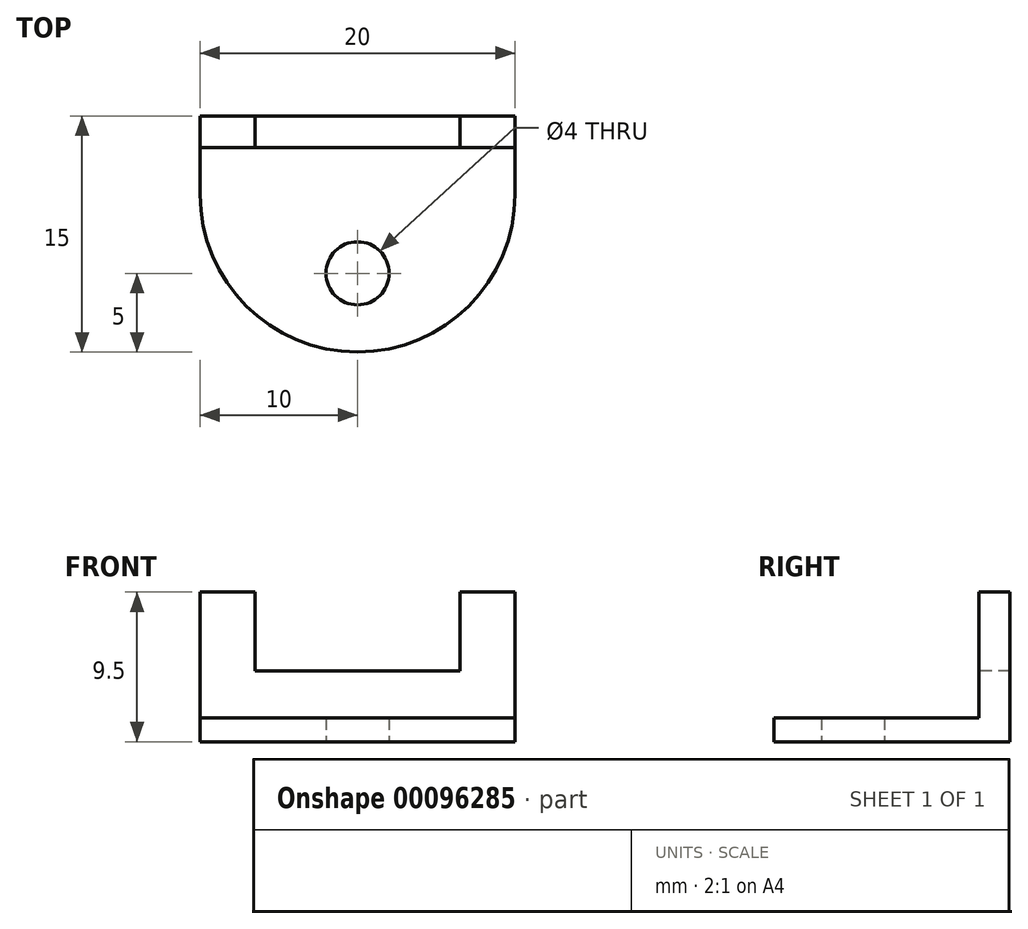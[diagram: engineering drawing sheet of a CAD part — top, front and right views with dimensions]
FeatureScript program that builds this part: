
annotation { "Feature Type Name" : "Feature", "Feature Type Description" : "" }
export const myFeature = defineFeature(function(context is Context, id is Id, definition is map)
    precondition{}
    {
        {
            var Q0;
            Q0=qCreatedBy(makeId("Top.planeOp"),FACE);
            var sketch = newSketch(context, id + "F0", { "sketchPlane" : qUnion([Q0])});
            skLineSegment(sketch, "E0.bottom", {"start": v(10, 2.5) * mm, "end": v(-10, 2.5) * mm});
            skLineSegment(sketch, "E0.top", {"start": v(10, -2.5) * mm, "end": v(-10, -2.5) * mm});
            skLineSegment(sketch, "E0.left", {"start": v(10, 2.5) * mm, "end": v(10, -2.5) * mm});
            skLineSegment(sketch, "E0.right", {"start": v(-10, 2.5) * mm, "end": v(-10, -2.5) * mm});
            skPoint(sketch, "E0.middle", {"position": v(0, 0) * mm});
            skArc(sketch, "E1", {"start": v(-10, -2.5) * mm, "mid": v(0, -12.5) * mm, "end": v(10, -2.5) * mm});
            skCircle(sketch, "E2", {"center": v(0, -7.5) * mm, "radius": 2 * mm});
            skSolve(sketch);
        }
        {
            var Q0;
            Q0=makeQuery(id+"F0.imprint","IMPRINT",FACE,{"disambiguationData":[TD([[makeQuery(id+"F0.imprint","IMPRINT",EDGE,{"derivedFrom":sQuery(id+"F0.wireOp",EDGE,"E0.bottom")}),1.0]])]});
            var Q1;
            Q1=makeQuery(id+"F0.imprint","IMPRINT",FACE,{"disambiguationData":[TD([[makeQuery(id+"F0.imprint","IMPRINT",EDGE,{"derivedFrom":sQuery(id+"F0.wireOp",EDGE,"E0.top")}),1.0]])]});
            extrude(context, id + "F1", {"entities" : qUnion([Q0, Q1]), "depth" : 1.5 * mm});
        }
        {
            var Q0;
            Q0=makeQuery(id+"F1.opExtrude","CAP_FACE",FACE,{"disambiguationData":[OSD([sQuery(id+"F0.wireOp",EDGE,"E0.bottom"),sQuery(id+"F0.wireOp",EDGE,"E0.left"),sQuery(id+"F0.wireOp",EDGE,"E0.right"),sQuery(id+"F0.wireOp",EDGE,"E1")])],"isStart":false});
            var sketch = newSketch(context, id + "F2", { "sketchPlane" : qUnion([Q0])});
            skLineSegment(sketch, "E3.bottom", {"start": v(-10, 2.5) * mm, "end": v(-6.5, 2.5) * mm});
            skLineSegment(sketch, "E3.top", {"start": v(-10, 0.5) * mm, "end": v(-6.5, 0.5) * mm});
            skLineSegment(sketch, "E3.left", {"start": v(-10, 2.5) * mm, "end": v(-10, 0.5) * mm});
            skLineSegment(sketch, "E3.right", {"start": v(-6.5, 2.5) * mm, "end": v(-6.5, 0.5) * mm});
            skLineSegment(sketch, "E4.MirrorCS", {"start": v(6.5, 2.5) * mm, "end": v(6.5, 0.5) * mm});
            skLineSegment(sketch, "E5.MirrorCS", {"start": v(10, 2.5) * mm, "end": v(10, 0.5) * mm});
            skLineSegment(sketch, "E6.MirrorCS", {"start": v(10, 0.5) * mm, "end": v(6.5, 0.5) * mm});
            skLineSegment(sketch, "E7.MirrorCS", {"start": v(10, 2.5) * mm, "end": v(6.5, 2.5) * mm});
            skSolve(sketch);
        }
        {
            var Q0;
            Q0=makeQuery(id+"F2.imprint","IMPRINT",FACE,{"disambiguationData":[TD([[makeQuery(id+"F2.imprint","IMPRINT",EDGE,{"derivedFrom":sQuery(id+"F2.wireOp",EDGE,"E3.bottom")}),1.0]])]});
            var Q1;
            Q1=makeQuery(id+"F2.imprint","IMPRINT",FACE,{"disambiguationData":[TD([[makeQuery(id+"F2.imprint","IMPRINT",EDGE,{"derivedFrom":sQuery(id+"F2.wireOp",EDGE,"E4.MirrorCS")}),1.0]])]});
            extrude(context, id + "F3", {"entities" : qUnion([Q0, Q1]), "operationType" : NewBodyOperationType.ADD, "depth" : 8 * mm});
        }
        {
            var Q0;
            Q0=makeQuery(id+"F1.opExtrude","CAP_FACE",FACE,{"disambiguationData":[OSD([sQuery(id+"F0.wireOp",EDGE,"E0.bottom"),sQuery(id+"F0.wireOp",EDGE,"E0.left"),sQuery(id+"F0.wireOp",EDGE,"E0.right"),sQuery(id+"F0.wireOp",EDGE,"E1"),sQuery(id+"F0.wireOp",EDGE,"E2")])],"isStart":false});
            var sketch = newSketch(context, id + "F4", { "sketchPlane" : qUnion([Q0])});
            skLineSegment(sketch, "E8.bottom", {"start": v(-6.5, 2.5) * mm, "end": v(6.5, 2.5) * mm});
            skLineSegment(sketch, "E8.top", {"start": v(-6.5, 0.5) * mm, "end": v(6.5, 0.5) * mm});
            skLineSegment(sketch, "E8.left", {"start": v(-6.5, 2.5) * mm, "end": v(-6.5, 0.5) * mm});
            skLineSegment(sketch, "E8.right", {"start": v(6.5, 2.5) * mm, "end": v(6.5, 0.5) * mm});
            skSolve(sketch);
        }
        {
            var Q0;
            Q0=makeQuery(id+"F4.imprint","IMPRINT",FACE,{"disambiguationData":[TD([[makeQuery(id+"F4.imprint","IMPRINT",EDGE,{"derivedFrom":sQuery(id+"F4.wireOp",EDGE,"E8.bottom")}),1.0]])]});
            extrude(context, id + "F5", {"entities" : qUnion([Q0]), "operationType" : NewBodyOperationType.ADD, "depth" : 3 * mm});
        }
    });
